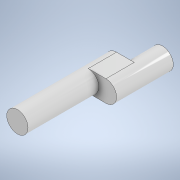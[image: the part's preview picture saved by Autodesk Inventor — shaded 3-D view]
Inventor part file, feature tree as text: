
AUTODESK INVENTOR PART (.ipt)
format: ipt  version: 2022 (Build 260153000, 153)  size: 119,296 bytes
history: native  units: mm
features: extrude x3, sketch x3
ambient origin geometry x8: Origin, YZ Plane, XZ Plane, XY Plane, X Axis, Y Axis, Z Axis, Center Point
bodies: 实体1 (feature_tree)
feature tree (6):
  extrude  "拉伸1"  Depth=4.0mm TaperAngle=0.0deg
  extrude  "拉伸2"  Depth=4.0mm TaperAngle=0.0deg
  extrude  "拉伸3"  [1 undecoded]
  sketch  "草图1"  dims[d0=3.0mm d1=4.0mm d2=0.0mm]
  sketch  "草图2"  dims[d3=2.5mm d4=4.0mm d5=0.0mm]
  sketch  "草图3"  dims[d6=10.0mm d7=0.0mm]
note: 1 required parameter value undecoded (feature->parameter linkage not recoverable at this tier; creation-order binding heuristic only, values carry confidence <= 0.55)
